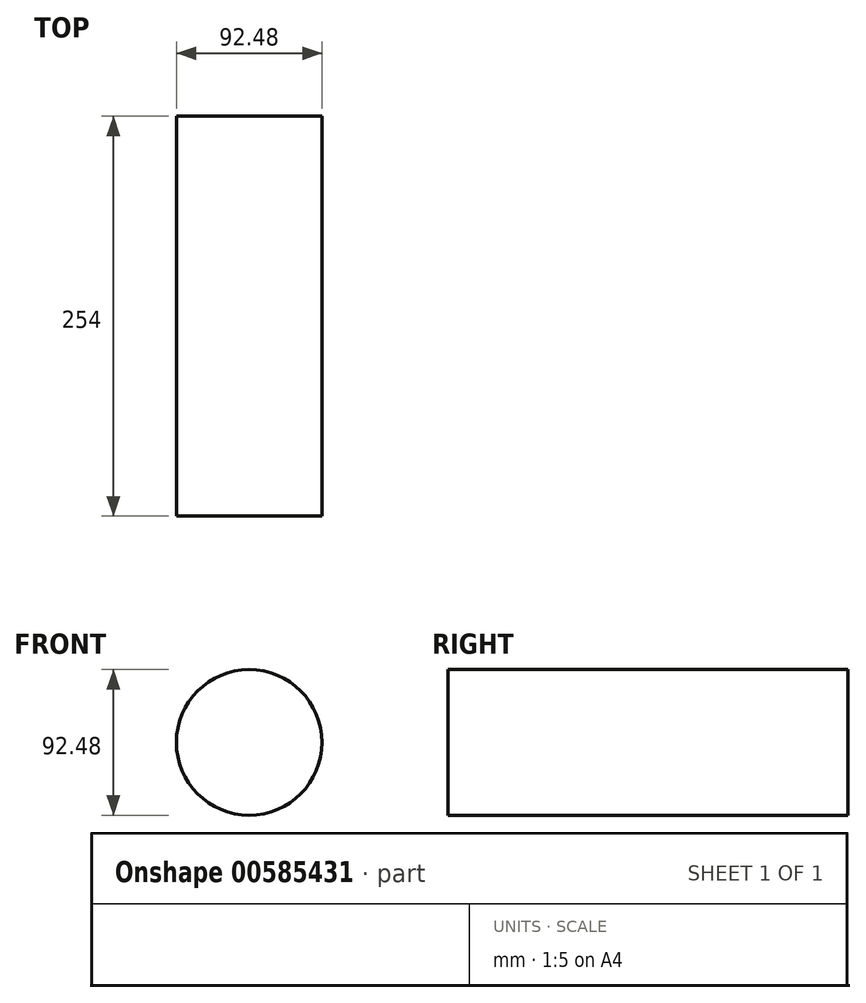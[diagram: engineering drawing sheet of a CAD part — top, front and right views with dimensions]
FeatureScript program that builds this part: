
annotation { "Feature Type Name" : "Feature", "Feature Type Description" : "" }
export const myFeature = defineFeature(function(context is Context, id is Id, definition is map)
    precondition{}
    {
        {
            var Q0;
            Q0=qCreatedBy(makeId("Front.planeOp"),FACE);
            var sketch = newSketch(context, id + "F0", { "sketchPlane" : qUnion([Q0])});
            skCircle(sketch, "E0", {"center": v(0, 0) * mm, "radius": 46.24 * mm});
            skSolve(sketch);
        }
        {
            var Q0;
            Q0=makeQuery(id+"F0.imprint","IMPRINT",FACE,{"disambiguationData":[TD([[makeQuery(id+"F0.imprint","IMPRINT",EDGE,{"derivedFrom":sQuery(id+"F0.wireOp",EDGE,"E0")}),1.0]])]});
            extrude(context, id + "F1", {"entities" : qUnion([Q0]), "depth" : 254 * mm, "offsetDistance" : 25.4 * mm});
        }
    });
